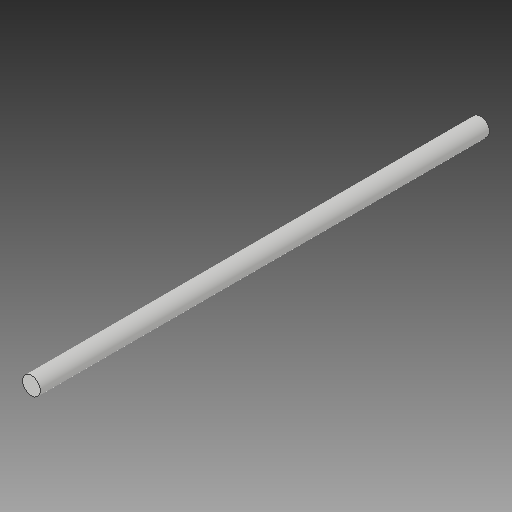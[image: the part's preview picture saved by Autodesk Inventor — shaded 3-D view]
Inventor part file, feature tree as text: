
AUTODESK INVENTOR PART (.ipt)
format: ipt  version: 2018 (Build 220112000, 112)  size: 89,088 bytes
history: native  units: mm
features: extrude x1, sketch x1
ambient origin geometry x8: Origin, YZ Plane, XZ Plane, XY Plane, X Axis, Y Axis, Z Axis, Center Point
bodies: Solid1 (feature_tree)
feature tree (2):
  extrude  "Extrusion1"  Depth=250.0mm TaperAngle=0.0deg
  sketch  "Sketch1"  dims[d0=10.0mm d1=250.0mm d2=0.0mm]
